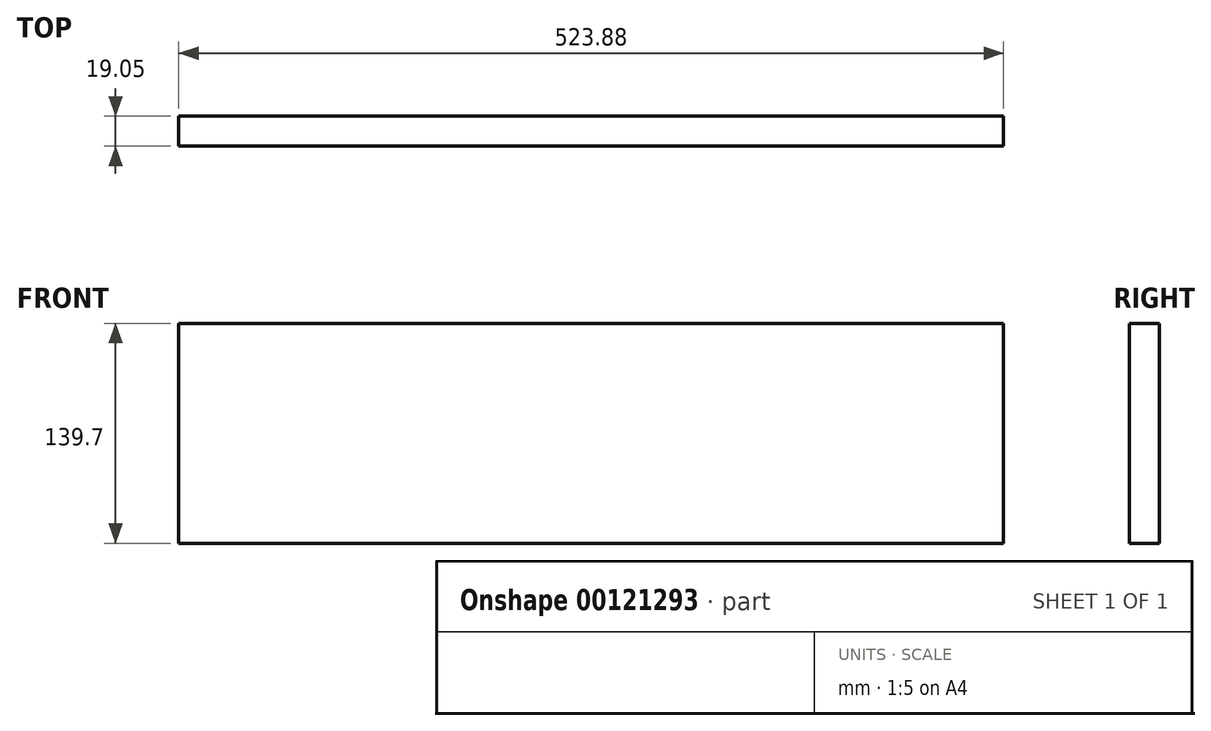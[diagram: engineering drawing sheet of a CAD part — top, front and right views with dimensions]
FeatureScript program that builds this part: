
annotation { "Feature Type Name" : "Feature", "Feature Type Description" : "" }
export const myFeature = defineFeature(function(context is Context, id is Id, definition is map)
    precondition{}
    {
        {
            var Q0;
            Q0=qCreatedBy(makeId("Front.planeOp"),FACE);
            var sketch = newSketch(context, id + "F0", { "sketchPlane" : qUnion([Q0])});
            skLineSegment(sketch, "E0.bottom", {"start": v(0, 0) * mm, "end": v(523.88, 0) * mm});
            skLineSegment(sketch, "E0.top", {"start": v(0, 139.7) * mm, "end": v(523.88, 139.7) * mm});
            skLineSegment(sketch, "E0.left", {"start": v(0, 0) * mm, "end": v(0, 139.7) * mm});
            skLineSegment(sketch, "E0.right", {"start": v(523.88, 0) * mm, "end": v(523.88, 139.7) * mm});
            skSolve(sketch);
        }
        {
            var Q0;
            Q0=makeQuery(id+"F0.imprint","IMPRINT",FACE,{"disambiguationData":[TD([[makeQuery(id+"F0.imprint","IMPRINT",EDGE,{"derivedFrom":sQuery(id+"F0.wireOp",EDGE,"E0.bottom")}),1.0]])]});
            extrude(context, id + "F1", {"entities" : qUnion([Q0]), "depth" : 19.05 * mm});
        }
    });
